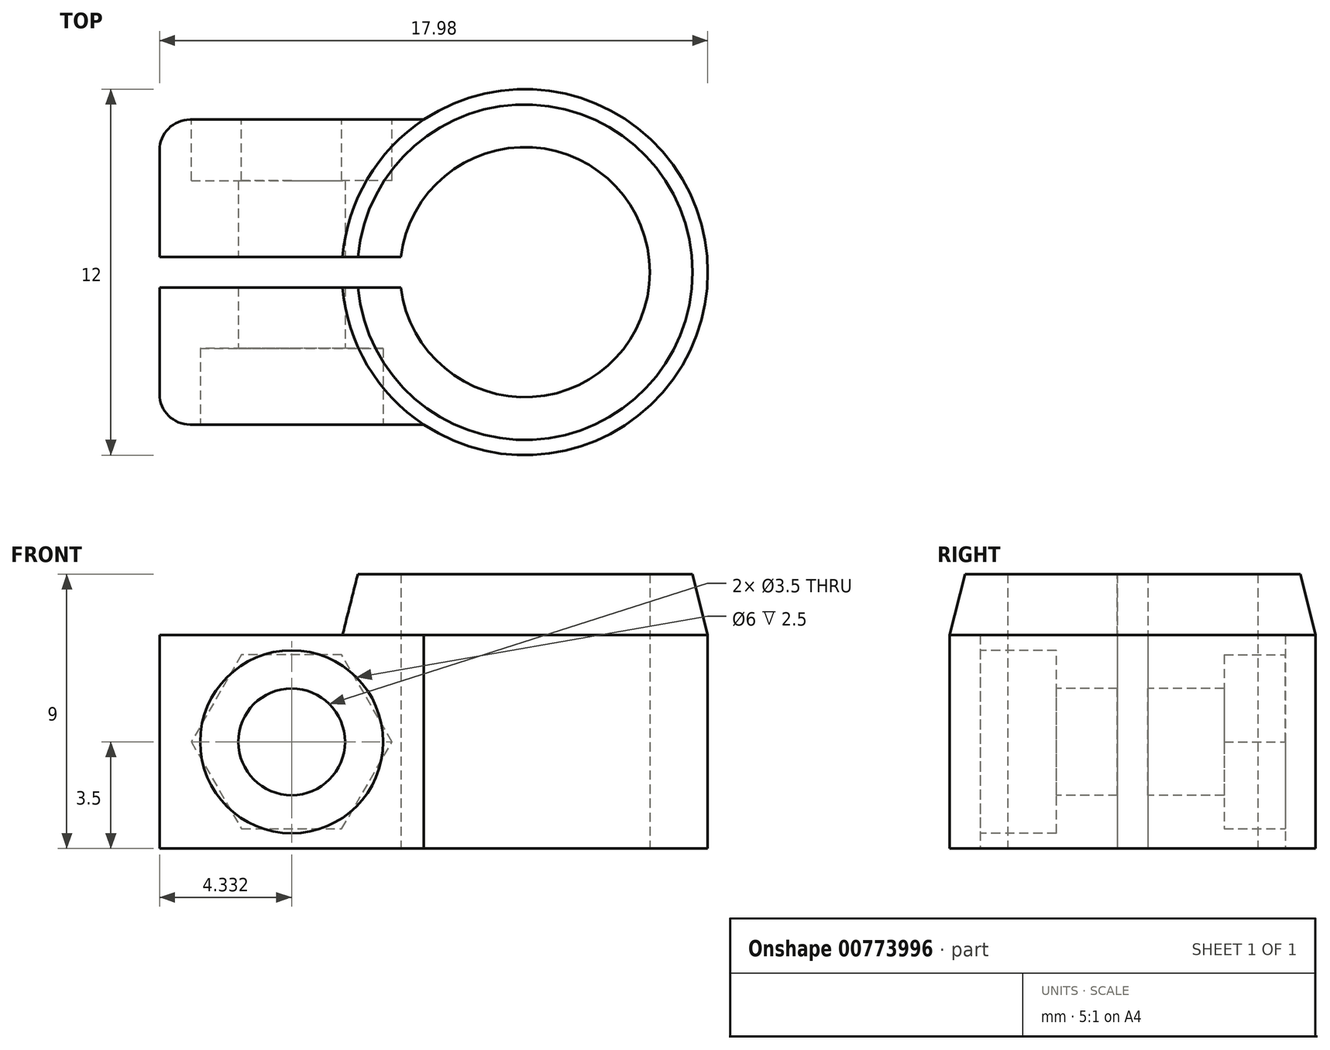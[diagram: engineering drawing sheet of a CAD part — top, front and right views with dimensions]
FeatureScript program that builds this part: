
annotation { "Feature Type Name" : "Feature", "Feature Type Description" : "" }
export const myFeature = defineFeature(function(context is Context, id is Id, definition is map)
    precondition{}
    {
        {
            var Q0;
            Q0=qCreatedBy(makeId("Top.planeOp"),FACE);
            var sketch = newSketch(context, id + "F0", { "sketchPlane" : qUnion([Q0])});
            skArc(sketch, "E0", {"start": v(-4.07, -0.5) * mm, "mid": v(4.1, 0) * mm, "end": v(-4.07, 0.5) * mm});
            skArc(sketch, "E1", {"start": v(-5.98, -0.5) * mm, "mid": v(6, 0) * mm, "end": v(-5.98, 0.5) * mm});
            skLineSegment(sketch, "E2", {"start": v(-4.07, -0.5) * mm, "end": v(-5.98, -0.5) * mm});
            skLineSegment(sketch, "E3", {"start": v(-4.07, 0.5) * mm, "end": v(-5.98, 0.5) * mm});
            skLineSegment(sketch, "E4", {"start": v(-4.07, 0.5) * mm, "end": v(-4.07, -0.5) * mm, "construction": true});
            skPoint(sketch, "E5", {"position": v(-4.07, 0) * mm});
            skLineSegment(sketch, "E6", {"start": v(-5.98, 0.5) * mm, "end": v(-11.98, 0.5) * mm});
            skLineSegment(sketch, "E7", {"start": v(-11.98, 0.5) * mm, "end": v(-11.98, 5) * mm});
            skLineSegment(sketch, "E8", {"start": v(-11.98, 5) * mm, "end": v(-3.32, 5) * mm});
            skLineSegment(sketch, "E9", {"start": v(-5.98, -0.5) * mm, "end": v(-11.98, -0.5) * mm});
            skLineSegment(sketch, "E10", {"start": v(-11.98, -0.5) * mm, "end": v(-11.98, -5) * mm});
            skLineSegment(sketch, "E11", {"start": v(-11.98, -5) * mm, "end": v(-3.32, -5) * mm});
            skSolve(sketch);
        }
        {
            var Q0;
            Q0=makeQuery(id+"F0.imprint","IMPRINT",FACE,{"disambiguationData":[TD([[makeQuery(id+"F0.imprint","IMPRINT",EDGE,{"derivedFrom":sQuery(id+"F0.wireOp",EDGE,"E0")}),-1.0]])]});
            extrude(context, id + "F1", {"entities" : qUnion([Q0]), "depth" : 9 * mm, "offsetDistance" : 25 * mm});
        }
        {
            var Q0;
            {var subQ0=sQuery(id+"F0.wireOp",EDGE,"E6");Q0=makeQuery(id+"F0.imprint","IMPRINT",FACE,{"disambiguationData":[TD([[makeQuery(id+"F0.imprint","IMPRINT",EDGE,{"derivedFrom":subQ0}),-1.0]])]});}
            var Q1;
            {var subQ0=sQuery(id+"F0.wireOp",EDGE,"E9");Q1=makeQuery(id+"F0.imprint","IMPRINT",FACE,{"disambiguationData":[TD([[makeQuery(id+"F0.imprint","IMPRINT",EDGE,{"derivedFrom":subQ0}),1.0]])]});}
            extrude(context, id + "F2", {"entities" : qUnion([Q0, Q1]), "operationType" : NewBodyOperationType.ADD, "depth" : 7 * mm, "offsetDistance" : 25 * mm});
        }
        {
            var Q0;
            Q0=makeQuery(id+"F1.opExtrude","SWEPT_FACE",FACE,{"disambiguationData":[OSD([sQuery(id+"F0.wireOp",EDGE,"E3")])]});
            cPlane(context, id + "F3", {"entities" : qUnion([Q0]), "cplaneType" : CPlaneType.OFFSET, "offset" : 10 * mm, "width" : 150 * mm, "height" : 150 * mm});
        }
        {
            var Q0;
            Q0=makeQuery(id+"F1.opExtrude","SWEPT_FACE",FACE,{"disambiguationData":[OSD([sQuery(id+"F0.wireOp",EDGE,"E2")])]});
            cPlane(context, id + "F4", {"entities" : qUnion([Q0]), "cplaneType" : CPlaneType.OFFSET, "offset" : 10 * mm, "width" : 150 * mm, "height" : 150 * mm});
        }
        {
            var Q0;
            Q0=qCreatedBy(id+"F3.planeOp",FACE);
            var sketch = newSketch(context, id + "F5", { "sketchPlane" : qUnion([Q0])});
            skLineSegment(sketch, "E12", {"start": v(-7.65, 7) * mm, "end": v(-7.65, 0) * mm, "construction": true});
            skPoint(sketch, "E13", {"position": v(-7.65, 3.5) * mm});
            skLineSegment(sketch, "E14.0.0", {"start": v(-11.98, 0) * mm, "end": v(-3.32, 0) * mm});
            skLineSegment(sketch, "E14.0.1", {"start": v(-3.32, 0) * mm, "end": v(-3.32, 7) * mm});
            skLineSegment(sketch, "E14.0.2", {"start": v(-3.32, 7) * mm, "end": v(-11.98, 7) * mm});
            skLineSegment(sketch, "E14.0.3", {"start": v(-11.98, 7) * mm, "end": v(-11.98, 0) * mm});
            skSolve(sketch);
        }
        {
            var Q0;
            Q0=qCreatedBy(id+"F4.planeOp",FACE);
            var sketch = newSketch(context, id + "F6", { "sketchPlane" : qUnion([Q0])});
            skCircle(sketch, "E15.cCircle", {"center": v(7.65, 3.5) * mm, "radius": 2.85 * mm, "construction": true});
            skLineSegment(sketch, "E15.0", {"start": v(9.3, 0.65) * mm, "end": v(6, 0.65) * mm});
            skLineSegment(sketch, "E15.1", {"start": v(6, 0.65) * mm, "end": v(4.36, 3.5) * mm});
            skLineSegment(sketch, "E15.2", {"start": v(4.36, 3.5) * mm, "end": v(6, 6.35) * mm});
            skLineSegment(sketch, "E15.3", {"start": v(6, 6.35) * mm, "end": v(9.3, 6.35) * mm});
            skLineSegment(sketch, "E15.4", {"start": v(9.3, 6.35) * mm, "end": v(10.94, 3.5) * mm});
            skLineSegment(sketch, "E15.5", {"start": v(10.94, 3.5) * mm, "end": v(9.3, 0.65) * mm});
            skPoint(sketch, "E15.0.midPoint", {"position": v(7.65, 0.65) * mm});
            skSolve(sketch);
        }
        {
            var Q0;
            Q0=sQuery(id+"F5.wireOp",VERTEX,"E13");
            var Q1;
            Q1=makeQuery(id+"F1.opExtrude","SWEPT_BODY",BODY,{"disambiguationData":[OSD([sQuery(id+"F0.wireOp",EDGE,"E0"),sQuery(id+"F0.wireOp",EDGE,"E1"),sQuery(id+"F0.wireOp",EDGE,"E2"),sQuery(id+"F0.wireOp",EDGE,"E3")])]});
            hole(context, id + "F7", {"style" : HoleStyle.C_BORE, "endStyle" : HoleEndStyle.THROUGH, "holeDiameter" : 3.5 * mm, "cBoreDiameter" : 6 * mm, "cBoreDepth" : 2.5 * mm, "majorDiameter" : 5 * mm, "tappedDepth" : 12 * mm, "tapClearance" : 3, "locations" : qUnion([Q0]), "scope" : qUnion([Q1])});
        }
        {
            var Q0;
            Q0 = qSketchRegion(id + "F6", true);
            extrude(context, id + "F8", {"entities" : qUnion([Q0]), "operationType" : NewBodyOperationType.REMOVE, "oppositeDirection" : true, "depth" : 6.5 * mm, "offsetDistance" : 25 * mm});
        }
        {
            var Q0;
            Q0=makeQuery(id+"F1.opExtrude","CAP_EDGE",EDGE,{"disambiguationData":[OSD([sQuery(id+"F0.wireOp",EDGE,"E1")])],"isStart":false});
            chamfer(context, id + "F9", {"entities" : qUnion([Q0]), "chamferType" : ChamferType.TWO_OFFSETS, "width1" : .5 * mm, "oppositeDirection" : false, "width2" : 2 * mm, "tangentPropagation" : true});
        }
        {
            var Q0;
            Q0=makeQuery(id+"F2.opExtrude","SWEPT_EDGE",EDGE,{"disambiguationData":[OSD([sQuery(id+"F0.wireOp",EDGE,"E1"),sQuery(id+"F0.wireOp",EDGE,"E11")])]});
            var Q1;
            Q1=makeQuery(id+"F2.opExtrude","SWEPT_EDGE",EDGE,{"disambiguationData":[OSD([sQuery(id+"F0.wireOp",EDGE,"E10"),sQuery(id+"F0.wireOp",EDGE,"E11")])]});
            var Q2;
            Q2=makeQuery(id+"F2.opExtrude","SWEPT_EDGE",EDGE,{"disambiguationData":[OSD([sQuery(id+"F0.wireOp",EDGE,"E7"),sQuery(id+"F0.wireOp",EDGE,"E8")])]});
            var Q3;
            Q3=makeQuery(id+"F2.opExtrude","SWEPT_EDGE",EDGE,{"disambiguationData":[OSD([sQuery(id+"F0.wireOp",EDGE,"E1"),sQuery(id+"F0.wireOp",EDGE,"E8")])]});
            fillet(context, id + "F10", {"entities" : qUnion([Q0, Q1, Q2, Q3]), "radius" : 1 * mm, "tangentPropagation" : true, "allowEdgeOverflow" : false});
        }
    });
